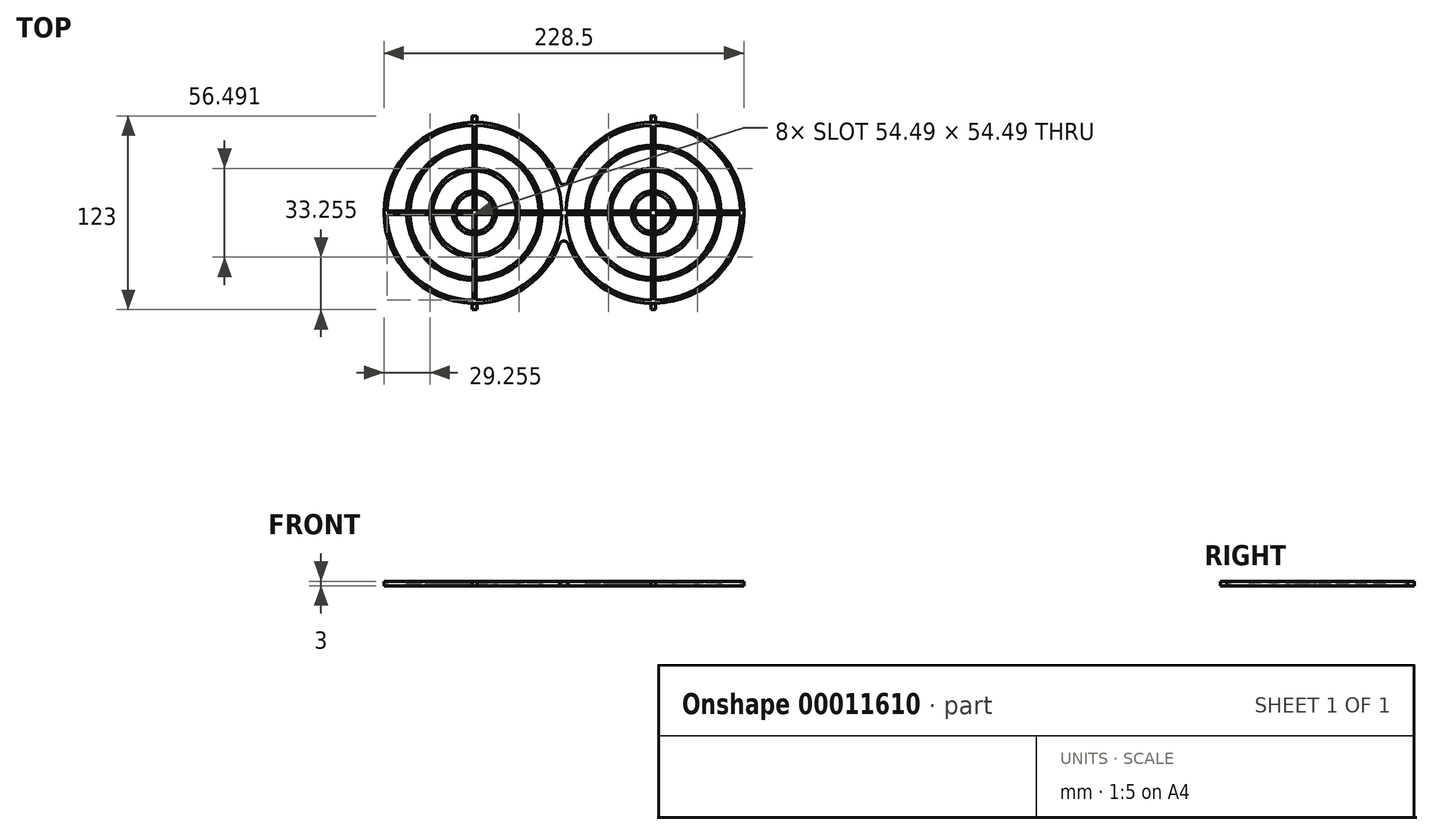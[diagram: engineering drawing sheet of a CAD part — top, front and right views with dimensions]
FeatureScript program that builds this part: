
annotation { "Feature Type Name" : "Feature", "Feature Type Description" : "" }
export const myFeature = defineFeature(function(context is Context, id is Id, definition is map)
    precondition{}
    {
        {
            var Q0;
            Q0=qCreatedBy(makeId("Top.planeOp"),FACE);
            var sketch = newSketch(context, id + "F0", { "sketchPlane" : qUnion([Q0])});
            skArc(sketch, "E0", {"start": v(-35.15, 19.67) * mm, "mid": v(-55.59, 46.67) * mm, "end": v(-87.68, 57.48) * mm});
            skArc(sketch, "E1", {"start": v(-29.71, -19.67) * mm, "mid": v(-9.27, -46.67) * mm, "end": v(22.82, -57.48) * mm});
            skArc(sketch, "E2", {"start": v(-35.15, 19.67) * mm, "mid": v(-32.43, 17.94) * mm, "end": v(-29.71, 19.67) * mm});
            skArc(sketch, "E3", {"start": v(-29.71, -19.67) * mm, "mid": v(-32.43, -17.94) * mm, "end": v(-35.15, -19.67) * mm});
            skArc(sketch, "E4", {"start": v(-31.17, -1) * mm, "mid": v(-14.92, -39.24) * mm, "end": v(23.32, -55.5) * mm});
            skArc(sketch, "E5", {"start": v(25.32, -42.99) * mm, "mid": v(54.73, -30.4) * mm, "end": v(67.3, -1) * mm});
            skArc(sketch, "E6", {"start": v(25.32, -40.99) * mm, "mid": v(53.31, -29) * mm, "end": v(65.3, -1) * mm});
            skArc(sketch, "E7", {"start": v(25.32, -28.48) * mm, "mid": v(44.47, -20.15) * mm, "end": v(52.8, -1) * mm});
            skArc(sketch, "E8", {"start": v(25.32, -26.48) * mm, "mid": v(43.06, -18.74) * mm, "end": v(50.8, -1) * mm});
            skArc(sketch, "E9", {"start": v(25.32, -13.96) * mm, "mid": v(34.22, -9.9) * mm, "end": v(38.28, -1) * mm});
            skArc(sketch, "E10", {"start": v(25.32, -11.96) * mm, "mid": v(32.8, -8.49) * mm, "end": v(36.28, -1) * mm});
            skArc(sketch, "E11", {"start": v(-90.18, 55.5) * mm, "mid": v(-128.42, 39.24) * mm, "end": v(-144.67, 1) * mm});
            skArc(sketch, "E12", {"start": v(-90.18, 42.99) * mm, "mid": v(-119.59, 30.4) * mm, "end": v(-132.17, 1) * mm});
            skArc(sketch, "E13", {"start": v(-90.18, 40.99) * mm, "mid": v(-118.17, 29) * mm, "end": v(-130.17, 1) * mm});
            skArc(sketch, "E14", {"start": v(-90.18, 28.48) * mm, "mid": v(-109.33, 20.15) * mm, "end": v(-117.66, 1) * mm});
            skArc(sketch, "E15", {"start": v(-90.18, 26.48) * mm, "mid": v(-107.92, 18.74) * mm, "end": v(-115.66, 1) * mm});
            skArc(sketch, "E16", {"start": v(-90.18, 13.96) * mm, "mid": v(-99.08, 9.9) * mm, "end": v(-103.14, 1) * mm});
            skArc(sketch, "E17", {"start": v(-90.18, 11.96) * mm, "mid": v(-97.67, 8.49) * mm, "end": v(-101.14, 1) * mm});
            skLineSegment(sketch, "E18.bottom", {"start": v(-88.18, 1) * mm, "end": v(-33.69, 1) * mm});
            skLineSegment(sketch, "E18.top", {"start": v(-88.18, -1) * mm, "end": v(-33.69, -1) * mm});
            skLineSegment(sketch, "E19.bottom", {"start": v(-90.18, 1) * mm, "end": v(-144.67, 1) * mm});
            skLineSegment(sketch, "E19.top", {"start": v(-90.18, -1) * mm, "end": v(-144.67, -1) * mm});
            skLineSegment(sketch, "E20.bottom", {"start": v(25.32, 1) * mm, "end": v(79.81, 1) * mm});
            skLineSegment(sketch, "E20.top", {"start": v(25.32, -1) * mm, "end": v(79.81, -1) * mm});
            skLineSegment(sketch, "E21.left", {"start": v(23.32, 1) * mm, "end": v(23.32, 55.5) * mm});
            skLineSegment(sketch, "E21.right", {"start": v(25.32, 1) * mm, "end": v(25.32, 55.5) * mm});
            skLineSegment(sketch, "E22.left", {"start": v(23.32, -1) * mm, "end": v(23.32, -55.5) * mm});
            skLineSegment(sketch, "E22.right", {"start": v(25.32, -1) * mm, "end": v(25.32, -55.5) * mm});
            skLineSegment(sketch, "E23.left", {"start": v(-88.18, 1) * mm, "end": v(-88.18, 55.5) * mm});
            skLineSegment(sketch, "E23.right", {"start": v(-90.18, 1) * mm, "end": v(-90.18, 55.5) * mm});
            skLineSegment(sketch, "E24.left", {"start": v(-90.18, -1) * mm, "end": v(-90.18, -55.5) * mm});
            skLineSegment(sketch, "E24.right", {"start": v(-88.18, -1) * mm, "end": v(-88.18, -55.5) * mm});
            skLineSegment(sketch, "E25.top", {"start": v(-87.68, 61.5) * mm, "end": v(-90.68, 61.5) * mm});
            skLineSegment(sketch, "E25.left", {"start": v(-87.68, 57.48) * mm, "end": v(-87.68, 61.5) * mm});
            skLineSegment(sketch, "E25.right", {"start": v(-90.68, 57.48) * mm, "end": v(-90.68, 61.5) * mm});
            skLineSegment(sketch, "E26.top", {"start": v(-87.68, -61.5) * mm, "end": v(-90.68, -61.5) * mm});
            skLineSegment(sketch, "E26.left", {"start": v(-87.68, -57.48) * mm, "end": v(-87.68, -61.5) * mm});
            skLineSegment(sketch, "E26.right", {"start": v(-90.68, -57.48) * mm, "end": v(-90.68, -61.5) * mm});
            skLineSegment(sketch, "E27.top", {"start": v(22.82, -61.5) * mm, "end": v(25.82, -61.5) * mm});
            skLineSegment(sketch, "E27.left", {"start": v(22.82, -57.48) * mm, "end": v(22.82, -61.5) * mm});
            skLineSegment(sketch, "E27.right", {"start": v(25.82, -57.48) * mm, "end": v(25.82, -61.5) * mm});
            skLineSegment(sketch, "E28.top", {"start": v(22.82, 61.5) * mm, "end": v(25.82, 61.5) * mm});
            skLineSegment(sketch, "E28.left", {"start": v(22.82, 57.48) * mm, "end": v(22.82, 61.5) * mm});
            skLineSegment(sketch, "E28.right", {"start": v(25.82, 57.48) * mm, "end": v(25.82, 61.5) * mm});
            skPoint(sketch, "E29.trimOffspring.end.orphan", {"position": v(-89.18, 61.5) * mm});
            skArc(sketch, "E30.trimOffspring", {"start": v(-90.68, 57.48) * mm, "mid": v(-146.68, 0) * mm, "end": v(-90.68, -57.48) * mm});
            skArc(sketch, "E31.trimOffspring", {"start": v(-101.14, -1) * mm, "mid": v(-97.67, -8.49) * mm, "end": v(-90.18, -11.96) * mm});
            skArc(sketch, "E32.trimOffspring", {"start": v(-103.14, -1) * mm, "mid": v(-99.08, -9.9) * mm, "end": v(-90.18, -13.96) * mm});
            skArc(sketch, "E33.trimOffspring", {"start": v(-115.66, -1) * mm, "mid": v(-107.92, -18.74) * mm, "end": v(-90.18, -26.48) * mm});
            skArc(sketch, "E34.trimOffspring", {"start": v(-117.66, -1) * mm, "mid": v(-109.33, -20.15) * mm, "end": v(-90.18, -28.48) * mm});
            skArc(sketch, "E35.trimOffspring", {"start": v(-144.67, -1) * mm, "mid": v(-128.42, -39.24) * mm, "end": v(-90.18, -55.5) * mm});
            skArc(sketch, "E36.trimOffspring", {"start": v(-132.17, -1) * mm, "mid": v(-119.59, -30.4) * mm, "end": v(-90.18, -42.99) * mm});
            skArc(sketch, "E37.trimOffspring", {"start": v(-130.17, -1) * mm, "mid": v(-118.17, -29) * mm, "end": v(-90.18, -40.99) * mm});
            skPoint(sketch, "E38.orphan", {"position": v(-89.18, -56) * mm});
            skPoint(sketch, "E39.orphan", {"position": v(-90.18, -56) * mm});
            skArc(sketch, "E40.trimOffspring", {"start": v(-88.18, -55.5) * mm, "mid": v(-49.94, -39.24) * mm, "end": v(-33.69, -1) * mm});
            skArc(sketch, "E41.trimOffspring", {"start": v(-87.68, -57.48) * mm, "mid": v(-55.59, -46.67) * mm, "end": v(-35.15, -19.67) * mm});
            skPoint(sketch, "E42.trimOffspring.end.orphan", {"position": v(-89.18, -61.5) * mm});
            skPoint(sketch, "E26.bottom.end.orphan", {"position": v(-88.18, -56) * mm});
            skArc(sketch, "E43.trimOffspring", {"start": v(-88.18, -11.96) * mm, "mid": v(-80.7, -8.49) * mm, "end": v(-77.22, -1) * mm});
            skArc(sketch, "E44.trimOffspring", {"start": v(-88.18, -13.96) * mm, "mid": v(-79.28, -9.9) * mm, "end": v(-75.22, -1) * mm});
            skArc(sketch, "E45.trimOffspring", {"start": v(-88.18, -26.48) * mm, "mid": v(-70.44, -18.74) * mm, "end": v(-62.7, -1) * mm});
            skArc(sketch, "E46.trimOffspring", {"start": v(-88.18, -28.48) * mm, "mid": v(-69.03, -20.15) * mm, "end": v(-60.7, -1) * mm});
            skArc(sketch, "E47.trimOffspring", {"start": v(-88.18, -42.99) * mm, "mid": v(-58.77, -30.4) * mm, "end": v(-46.2, -1) * mm});
            skArc(sketch, "E48.trimOffspring", {"start": v(-88.18, -40.99) * mm, "mid": v(-60.19, -29) * mm, "end": v(-48.2, -1) * mm});
            skArc(sketch, "E49.trimOffspring", {"start": v(-48.2, 1) * mm, "mid": v(-60.19, 29) * mm, "end": v(-88.18, 40.99) * mm});
            skArc(sketch, "E50.trimOffspring", {"start": v(-60.7, 1) * mm, "mid": v(-69.03, 20.15) * mm, "end": v(-88.18, 28.48) * mm});
            skArc(sketch, "E51.trimOffspring", {"start": v(-62.7, 1) * mm, "mid": v(-70.44, 18.74) * mm, "end": v(-88.18, 26.48) * mm});
            skArc(sketch, "E52.trimOffspring", {"start": v(-75.22, 1) * mm, "mid": v(-79.28, 9.9) * mm, "end": v(-88.18, 13.96) * mm});
            skArc(sketch, "E53.trimOffspring", {"start": v(-77.22, 1) * mm, "mid": v(-80.7, 8.49) * mm, "end": v(-88.18, 11.96) * mm});
            skArc(sketch, "E54.trimOffspring", {"start": v(-46.2, 1) * mm, "mid": v(-58.77, 30.4) * mm, "end": v(-88.18, 42.99) * mm});
            skArc(sketch, "E55.trimOffspring", {"start": v(-33.69, 1) * mm, "mid": v(-49.94, 39.24) * mm, "end": v(-88.18, 55.5) * mm});
            skLineSegment(sketch, "E56.trimOffspring", {"start": v(-31.17, 1) * mm, "end": v(23.32, 1) * mm});
            skLineSegment(sketch, "E57.trimOffspring", {"start": v(-31.17, -1) * mm, "end": v(23.32, -1) * mm});
            skArc(sketch, "E58.trimOffspring", {"start": v(25.32, -55.5) * mm, "mid": v(63.56, -39.24) * mm, "end": v(79.81, -1) * mm});
            skPoint(sketch, "E59.orphan", {"position": v(25.32, -56) * mm});
            skPoint(sketch, "E60.orphan", {"position": v(24.32, -56) * mm});
            skPoint(sketch, "E61.end.orphan", {"position": v(24.32, -61.5) * mm});
            skArc(sketch, "E62.trimOffspring", {"start": v(25.82, -57.48) * mm, "mid": v(81.82, 0) * mm, "end": v(25.82, 57.48) * mm});
            skPoint(sketch, "E63.start.orphan", {"position": v(23.32, -56) * mm});
            skArc(sketch, "E64.trimOffspring", {"start": v(23.32, 13.96) * mm, "mid": v(14.42, 9.9) * mm, "end": v(10.36, 1) * mm});
            skArc(sketch, "E65.trimOffspring", {"start": v(23.32, 11.96) * mm, "mid": v(15.83, 8.49) * mm, "end": v(12.36, 1) * mm});
            skArc(sketch, "E66.trimOffspring", {"start": v(23.32, 28.48) * mm, "mid": v(4.17, 20.15) * mm, "end": v(-4.16, 1) * mm});
            skArc(sketch, "E67.trimOffspring", {"start": v(23.32, 26.48) * mm, "mid": v(5.58, 18.74) * mm, "end": v(-2.16, 1) * mm});
            skArc(sketch, "E68.trimOffspring", {"start": v(23.32, 42.99) * mm, "mid": v(-6.09, 30.4) * mm, "end": v(-18.67, 1) * mm});
            skArc(sketch, "E69.trimOffspring", {"start": v(23.32, 40.99) * mm, "mid": v(-4.67, 29) * mm, "end": v(-16.67, 1) * mm});
            skArc(sketch, "E70.trimOffspring", {"start": v(23.32, 55.5) * mm, "mid": v(-14.92, 39.24) * mm, "end": v(-31.17, 1) * mm});
            skPoint(sketch, "E71.trimOffspring.end.orphan", {"position": v(24.32, 61.5) * mm});
            skArc(sketch, "E72.trimOffspring", {"start": v(22.82, 57.48) * mm, "mid": v(-9.27, 46.67) * mm, "end": v(-29.71, 19.67) * mm});
            skArc(sketch, "E73.trimOffspring", {"start": v(65.3, 1) * mm, "mid": v(53.31, 29) * mm, "end": v(25.32, 40.99) * mm});
            skArc(sketch, "E74.trimOffspring", {"start": v(67.3, 1) * mm, "mid": v(54.73, 30.4) * mm, "end": v(25.32, 42.99) * mm});
            skArc(sketch, "E75.trimOffspring", {"start": v(79.81, 1) * mm, "mid": v(63.56, 39.24) * mm, "end": v(25.32, 55.5) * mm});
            skArc(sketch, "E76.trimOffspring", {"start": v(52.8, 1) * mm, "mid": v(44.47, 20.15) * mm, "end": v(25.32, 28.48) * mm});
            skArc(sketch, "E77.trimOffspring", {"start": v(50.8, 1) * mm, "mid": v(43.06, 18.74) * mm, "end": v(25.32, 26.48) * mm});
            skArc(sketch, "E78.trimOffspring", {"start": v(38.28, 1) * mm, "mid": v(34.22, 9.9) * mm, "end": v(25.32, 13.96) * mm});
            skArc(sketch, "E79.trimOffspring", {"start": v(36.28, 1) * mm, "mid": v(32.8, 8.49) * mm, "end": v(25.32, 11.96) * mm});
            skArc(sketch, "E80.trimOffspring", {"start": v(12.36, -1) * mm, "mid": v(15.83, -8.49) * mm, "end": v(23.32, -11.96) * mm});
            skArc(sketch, "E81.trimOffspring", {"start": v(10.36, -1) * mm, "mid": v(14.42, -9.9) * mm, "end": v(23.32, -13.96) * mm});
            skArc(sketch, "E82.trimOffspring", {"start": v(-2.16, -1) * mm, "mid": v(5.58, -18.74) * mm, "end": v(23.32, -26.48) * mm});
            skArc(sketch, "E83.trimOffspring", {"start": v(-4.16, -1) * mm, "mid": v(4.17, -20.15) * mm, "end": v(23.32, -28.48) * mm});
            skArc(sketch, "E84.trimOffspring", {"start": v(-16.67, -1) * mm, "mid": v(-4.67, -29) * mm, "end": v(23.32, -40.99) * mm});
            skArc(sketch, "E85.trimOffspring", {"start": v(-18.67, -1) * mm, "mid": v(-6.09, -30.4) * mm, "end": v(23.32, -42.99) * mm});
            skSolve(sketch);
        }
        {
            var Q0;
            Q0=makeQuery(id+"F0.imprint","IMPRINT",FACE,{"disambiguationData":[TD([[makeQuery(id+"F0.imprint","IMPRINT",EDGE,{"derivedFrom":sQuery(id+"F0.wireOp",EDGE,"E0")}),1.0]])]});
            extrude(context, id + "F1", {"entities" : qUnion([Q0]), "depth" : 3 * mm});
        }
        {
            var Q0;
            {var subQ2=sQuery(id+"F0.wireOp",EDGE,"E12");Q0=makeQuery(id+"F0.imprint","IMPRINT",FACE,{"disambiguationData":[TD([[makeQuery(id+"F0.imprint","IMPRINT",EDGE,{"derivedFrom":subQ2}),1.0]])]});}
            var Q1;
            {var subQ2=sQuery(id+"F0.wireOp",EDGE,"E14");Q1=makeQuery(id+"F0.imprint","IMPRINT",FACE,{"disambiguationData":[TD([[makeQuery(id+"F0.imprint","IMPRINT",EDGE,{"derivedFrom":subQ2}),1.0]])]});}
            var Q2;
            {var subQ2=sQuery(id+"F0.wireOp",EDGE,"E16");Q2=makeQuery(id+"F0.imprint","IMPRINT",FACE,{"disambiguationData":[TD([[makeQuery(id+"F0.imprint","IMPRINT",EDGE,{"derivedFrom":subQ2}),1.0]])]});}
            var Q3;
            {var subQ1=sQuery(id+"F0.wireOp",EDGE,"E52.trimOffspring");Q3=makeQuery(id+"F0.imprint","IMPRINT",FACE,{"disambiguationData":[TD([[makeQuery(id+"F0.imprint","IMPRINT",EDGE,{"derivedFrom":subQ1}),1.0]])]});}
            var Q4;
            {var subQ1=sQuery(id+"F0.wireOp",EDGE,"E50.trimOffspring");Q4=makeQuery(id+"F0.imprint","IMPRINT",FACE,{"disambiguationData":[TD([[makeQuery(id+"F0.imprint","IMPRINT",EDGE,{"derivedFrom":subQ1}),1.0]])]});}
            var Q5;
            {var subQ1=sQuery(id+"F0.wireOp",EDGE,"E49.trimOffspring");Q5=makeQuery(id+"F0.imprint","IMPRINT",FACE,{"disambiguationData":[TD([[makeQuery(id+"F0.imprint","IMPRINT",EDGE,{"derivedFrom":subQ1}),-1.0]])]});}
            var Q6;
            {var subQ1=sQuery(id+"F0.wireOp",EDGE,"E43.trimOffspring");Q6=makeQuery(id+"F0.imprint","IMPRINT",FACE,{"disambiguationData":[TD([[makeQuery(id+"F0.imprint","IMPRINT",EDGE,{"derivedFrom":subQ1}),-1.0]])]});}
            var Q7;
            {var subQ1=sQuery(id+"F0.wireOp",EDGE,"E45.trimOffspring");Q7=makeQuery(id+"F0.imprint","IMPRINT",FACE,{"disambiguationData":[TD([[makeQuery(id+"F0.imprint","IMPRINT",EDGE,{"derivedFrom":subQ1}),-1.0]])]});}
            var Q8;
            {var subQ0=sQuery(id+"F0.wireOp",EDGE,"E47.trimOffspring");Q8=makeQuery(id+"F0.imprint","IMPRINT",FACE,{"disambiguationData":[TD([[makeQuery(id+"F0.imprint","IMPRINT",EDGE,{"derivedFrom":subQ0}),1.0]])]});}
            var Q9;
            {var subQ1=sQuery(id+"F0.wireOp",EDGE,"E31.trimOffspring");Q9=makeQuery(id+"F0.imprint","IMPRINT",FACE,{"disambiguationData":[TD([[makeQuery(id+"F0.imprint","IMPRINT",EDGE,{"derivedFrom":subQ1}),-1.0]])]});}
            var Q10;
            {var subQ1=sQuery(id+"F0.wireOp",EDGE,"E33.trimOffspring");Q10=makeQuery(id+"F0.imprint","IMPRINT",FACE,{"disambiguationData":[TD([[makeQuery(id+"F0.imprint","IMPRINT",EDGE,{"derivedFrom":subQ1}),-1.0]])]});}
            var Q11;
            {var subQ1=sQuery(id+"F0.wireOp",EDGE,"E36.trimOffspring");Q11=makeQuery(id+"F0.imprint","IMPRINT",FACE,{"disambiguationData":[TD([[makeQuery(id+"F0.imprint","IMPRINT",EDGE,{"derivedFrom":subQ1}),1.0]])]});}
            var Q12;
            {var subQ2=sQuery(id+"F0.wireOp",EDGE,"E68.trimOffspring");Q12=makeQuery(id+"F0.imprint","IMPRINT",FACE,{"disambiguationData":[TD([[makeQuery(id+"F0.imprint","IMPRINT",EDGE,{"derivedFrom":subQ2}),1.0]])]});}
            var Q13;
            {var subQ0=sQuery(id+"F0.wireOp",EDGE,"E66.trimOffspring");Q13=makeQuery(id+"F0.imprint","IMPRINT",FACE,{"disambiguationData":[TD([[makeQuery(id+"F0.imprint","IMPRINT",EDGE,{"derivedFrom":subQ0}),1.0]])]});}
            var Q14;
            {var subQ1=sQuery(id+"F0.wireOp",EDGE,"E73.trimOffspring");Q14=makeQuery(id+"F0.imprint","IMPRINT",FACE,{"disambiguationData":[TD([[makeQuery(id+"F0.imprint","IMPRINT",EDGE,{"derivedFrom":subQ1}),-1.0]])]});}
            var Q15;
            {var subQ1=sQuery(id+"F0.wireOp",EDGE,"E76.trimOffspring");Q15=makeQuery(id+"F0.imprint","IMPRINT",FACE,{"disambiguationData":[TD([[makeQuery(id+"F0.imprint","IMPRINT",EDGE,{"derivedFrom":subQ1}),1.0]])]});}
            var Q16;
            {var subQ1=sQuery(id+"F0.wireOp",EDGE,"E78.trimOffspring");Q16=makeQuery(id+"F0.imprint","IMPRINT",FACE,{"disambiguationData":[TD([[makeQuery(id+"F0.imprint","IMPRINT",EDGE,{"derivedFrom":subQ1}),1.0]])]});}
            var Q17;
            {var subQ1=sQuery(id+"F0.wireOp",EDGE,"E64.trimOffspring");Q17=makeQuery(id+"F0.imprint","IMPRINT",FACE,{"disambiguationData":[TD([[makeQuery(id+"F0.imprint","IMPRINT",EDGE,{"derivedFrom":subQ1}),1.0]])]});}
            var Q18;
            {var subQ1=sQuery(id+"F0.wireOp",EDGE,"E80.trimOffspring");Q18=makeQuery(id+"F0.imprint","IMPRINT",FACE,{"disambiguationData":[TD([[makeQuery(id+"F0.imprint","IMPRINT",EDGE,{"derivedFrom":subQ1}),-1.0]])]});}
            var Q19;
            {var subQ1=sQuery(id+"F0.wireOp",EDGE,"E82.trimOffspring");Q19=makeQuery(id+"F0.imprint","IMPRINT",FACE,{"disambiguationData":[TD([[makeQuery(id+"F0.imprint","IMPRINT",EDGE,{"derivedFrom":subQ1}),-1.0]])]});}
            var Q20;
            {var subQ1=sQuery(id+"F0.wireOp",EDGE,"E84.trimOffspring");Q20=makeQuery(id+"F0.imprint","IMPRINT",FACE,{"disambiguationData":[TD([[makeQuery(id+"F0.imprint","IMPRINT",EDGE,{"derivedFrom":subQ1}),-1.0]])]});}
            var Q21;
            {var subQ2=sQuery(id+"F0.wireOp",EDGE,"E9");Q21=makeQuery(id+"F0.imprint","IMPRINT",FACE,{"disambiguationData":[TD([[makeQuery(id+"F0.imprint","IMPRINT",EDGE,{"derivedFrom":subQ2}),1.0]])]});}
            var Q22;
            {var subQ2=sQuery(id+"F0.wireOp",EDGE,"E7");Q22=makeQuery(id+"F0.imprint","IMPRINT",FACE,{"disambiguationData":[TD([[makeQuery(id+"F0.imprint","IMPRINT",EDGE,{"derivedFrom":subQ2}),1.0]])]});}
            var Q23;
            {var subQ2=sQuery(id+"F0.wireOp",EDGE,"E5");Q23=makeQuery(id+"F0.imprint","IMPRINT",FACE,{"disambiguationData":[TD([[makeQuery(id+"F0.imprint","IMPRINT",EDGE,{"derivedFrom":subQ2}),1.0]])]});}
            extrude(context, id + "F2", {"entities" : qUnion([Q0, Q1, Q2, Q3, Q4, Q5, Q6, Q7, Q8, Q9, Q10, Q11, Q12, Q13, Q14, Q15, Q16, Q17, Q18, Q19, Q20, Q21, Q22, Q23]), "operationType" : NewBodyOperationType.ADD, "depth" : 2 * mm});
        }
        {
            var Q0;
            Q0=makeQuery(id+"F1.opExtrude","SWEPT_FACE",FACE,{"disambiguationData":[OSD([sQuery(id+"F0.wireOp",EDGE,"E26.top")])]});
            var sketch = newSketch(context, id + "F3", { "sketchPlane" : qUnion([Q0])});
            skCircle(sketch, "E86", {"center": v(-89.18, 1.5) * mm, "radius": 1.5 * mm});
            skCircle(sketch, "E87", {"center": v(24.32, 1.5) * mm, "radius": 1.5 * mm});
            skLineSegment(sketch, "E88.bottom", {"start": v(22.82, 3) * mm, "end": v(25.82, 3) * mm});
            skLineSegment(sketch, "E88.top", {"start": v(22.82, 0) * mm, "end": v(25.82, 0) * mm});
            skLineSegment(sketch, "E88.left", {"start": v(22.82, 3) * mm, "end": v(22.82, 0) * mm});
            skLineSegment(sketch, "E88.right", {"start": v(25.82, 3) * mm, "end": v(25.82, 0) * mm});
            skLineSegment(sketch, "E89.bottom", {"start": v(-90.68, 3) * mm, "end": v(-87.68, 3) * mm});
            skLineSegment(sketch, "E89.top", {"start": v(-90.68, 0) * mm, "end": v(-87.68, 0) * mm});
            skLineSegment(sketch, "E89.left", {"start": v(-90.68, 3) * mm, "end": v(-90.68, 0) * mm});
            skLineSegment(sketch, "E89.right", {"start": v(-87.68, 3) * mm, "end": v(-87.68, 0) * mm});
            skSolve(sketch);
        }
        {
            var Q0;
            {var subQ1=sQuery(id+"F3.wireOp",EDGE,"E86");var subQ3=sQuery(id+"F3.wireOp",EDGE,"E89.bottom");var subQ5=makeQuery(id+"F3.imprint","INTERSECT",VERTEX,{"derivedFrom":[subQ1,subQ3]});Q0=makeQuery(id+"F3.imprint","IMPRINT",FACE,{"disambiguationData":[TD([[makeQuery(id+"F3.imprint","IMPRINT",EDGE,{"disambiguationData":[TD([[subQ5,-1.0]])],"derivedFrom":subQ1}),-1.0]])]});}
            var Q1;
            {var subQ1=sQuery(id+"F3.wireOp",EDGE,"E86");var subQ3=sQuery(id+"F3.wireOp",EDGE,"E89.bottom");var subQ5=makeQuery(id+"F3.imprint","INTERSECT",VERTEX,{"derivedFrom":[subQ1,subQ3]});Q1=makeQuery(id+"F3.imprint","IMPRINT",FACE,{"disambiguationData":[TD([[makeQuery(id+"F3.imprint","IMPRINT",EDGE,{"disambiguationData":[TD([[subQ5,1.0]])],"derivedFrom":subQ1}),-1.0]])]});}
            var Q2;
            {var subQ0=sQuery(id+"F3.wireOp",EDGE,"E89.right");var subQ1=sQuery(id+"F3.wireOp",EDGE,"E86");var subQ2=makeQuery(id+"F3.imprint","INTERSECT",VERTEX,{"derivedFrom":[subQ1,subQ0]});Q2=makeQuery(id+"F3.imprint","IMPRINT",FACE,{"disambiguationData":[TD([[makeQuery(id+"F3.imprint","IMPRINT",EDGE,{"disambiguationData":[TD([[subQ2,1.0]])],"derivedFrom":subQ1}),-1.0]])]});}
            var Q3;
            {var subQ0=sQuery(id+"F3.wireOp",EDGE,"E89.left");var subQ1=sQuery(id+"F3.wireOp",EDGE,"E86");var subQ2=makeQuery(id+"F3.imprint","INTERSECT",VERTEX,{"derivedFrom":[subQ1,subQ0]});Q3=makeQuery(id+"F3.imprint","IMPRINT",FACE,{"disambiguationData":[TD([[makeQuery(id+"F3.imprint","IMPRINT",EDGE,{"disambiguationData":[TD([[subQ2,-1.0]])],"derivedFrom":subQ1}),-1.0]])]});}
            var Q4;
            {var subQ1=sQuery(id+"F3.wireOp",EDGE,"E87");var subQ3=sQuery(id+"F3.wireOp",EDGE,"E88.bottom");var subQ5=makeQuery(id+"F3.imprint","INTERSECT",VERTEX,{"derivedFrom":[subQ1,subQ3]});Q4=makeQuery(id+"F3.imprint","IMPRINT",FACE,{"disambiguationData":[TD([[makeQuery(id+"F3.imprint","IMPRINT",EDGE,{"disambiguationData":[TD([[subQ5,-1.0]])],"derivedFrom":subQ1}),-1.0]])]});}
            var Q5;
            {var subQ1=sQuery(id+"F3.wireOp",EDGE,"E87");var subQ3=sQuery(id+"F3.wireOp",EDGE,"E88.bottom");var subQ5=makeQuery(id+"F3.imprint","INTERSECT",VERTEX,{"derivedFrom":[subQ1,subQ3]});Q5=makeQuery(id+"F3.imprint","IMPRINT",FACE,{"disambiguationData":[TD([[makeQuery(id+"F3.imprint","IMPRINT",EDGE,{"disambiguationData":[TD([[subQ5,1.0]])],"derivedFrom":subQ1}),-1.0]])]});}
            var Q6;
            {var subQ0=sQuery(id+"F3.wireOp",EDGE,"E88.right");var subQ1=sQuery(id+"F3.wireOp",EDGE,"E87");var subQ2=makeQuery(id+"F3.imprint","INTERSECT",VERTEX,{"derivedFrom":[subQ1,subQ0]});Q6=makeQuery(id+"F3.imprint","IMPRINT",FACE,{"disambiguationData":[TD([[makeQuery(id+"F3.imprint","IMPRINT",EDGE,{"disambiguationData":[TD([[subQ2,1.0]])],"derivedFrom":subQ1}),-1.0]])]});}
            var Q7;
            {var subQ0=sQuery(id+"F3.wireOp",EDGE,"E88.left");var subQ1=sQuery(id+"F3.wireOp",EDGE,"E87");var subQ2=makeQuery(id+"F3.imprint","INTERSECT",VERTEX,{"derivedFrom":[subQ1,subQ0]});Q7=makeQuery(id+"F3.imprint","IMPRINT",FACE,{"disambiguationData":[TD([[makeQuery(id+"F3.imprint","IMPRINT",EDGE,{"disambiguationData":[TD([[subQ2,-1.0]])],"derivedFrom":subQ1}),-1.0]])]});}
            extrude(context, id + "F4", {"entities" : qUnion([Q0, Q1, Q2, Q3, Q4, Q5, Q6, Q7]), "operationType" : NewBodyOperationType.REMOVE, "oppositeDirection" : true, "depth" : 4 * mm});
        }
        {
            var Q0;
            Q0=makeQuery(id+"F1.opExtrude","SWEPT_FACE",FACE,{"disambiguationData":[OSD([sQuery(id+"F0.wireOp",EDGE,"E28.top")])]});
            var sketch = newSketch(context, id + "F5", { "sketchPlane" : qUnion([Q0])});
            skCircle(sketch, "E90", {"center": v(-24.32, 1.5) * mm, "radius": 1.5 * mm});
            skCircle(sketch, "E91", {"center": v(89.18, 1.5) * mm, "radius": 1.5 * mm});
            skLineSegment(sketch, "E92.bottom", {"start": v(-25.82, 3) * mm, "end": v(-22.82, 3) * mm});
            skLineSegment(sketch, "E92.top", {"start": v(-25.82, 0) * mm, "end": v(-22.82, 0) * mm});
            skLineSegment(sketch, "E92.left", {"start": v(-25.82, 3) * mm, "end": v(-25.82, 0) * mm});
            skLineSegment(sketch, "E92.right", {"start": v(-22.82, 3) * mm, "end": v(-22.82, 0) * mm});
            skLineSegment(sketch, "E93.rect.bottom", {"start": v(87.68, 3) * mm, "end": v(90.68, 3) * mm});
            skLineSegment(sketch, "E93.rect.top", {"start": v(87.68, 0) * mm, "end": v(90.68, 0) * mm});
            skLineSegment(sketch, "E93.rect.left", {"start": v(87.68, 3) * mm, "end": v(87.68, 0) * mm});
            skLineSegment(sketch, "E93.rect.right", {"start": v(90.68, 3) * mm, "end": v(90.68, 0) * mm});
            skSolve(sketch);
        }
        {
            var Q0;
            {var subQ1=sQuery(id+"F5.wireOp",EDGE,"E90");var subQ3=sQuery(id+"F5.wireOp",EDGE,"E92.bottom");var subQ5=makeQuery(id+"F5.imprint","INTERSECT",VERTEX,{"derivedFrom":[subQ1,subQ3]});Q0=makeQuery(id+"F5.imprint","IMPRINT",FACE,{"disambiguationData":[TD([[makeQuery(id+"F5.imprint","IMPRINT",EDGE,{"disambiguationData":[TD([[subQ5,-1.0]])],"derivedFrom":subQ1}),-1.0]])]});}
            var Q1;
            {var subQ1=sQuery(id+"F5.wireOp",EDGE,"E90");var subQ3=sQuery(id+"F5.wireOp",EDGE,"E92.bottom");var subQ5=makeQuery(id+"F5.imprint","INTERSECT",VERTEX,{"derivedFrom":[subQ1,subQ3]});Q1=makeQuery(id+"F5.imprint","IMPRINT",FACE,{"disambiguationData":[TD([[makeQuery(id+"F5.imprint","IMPRINT",EDGE,{"disambiguationData":[TD([[subQ5,1.0]])],"derivedFrom":subQ1}),-1.0]])]});}
            var Q2;
            {var subQ0=sQuery(id+"F5.wireOp",EDGE,"E92.right");var subQ1=sQuery(id+"F5.wireOp",EDGE,"E90");var subQ2=makeQuery(id+"F5.imprint","INTERSECT",VERTEX,{"derivedFrom":[subQ1,subQ0]});Q2=makeQuery(id+"F5.imprint","IMPRINT",FACE,{"disambiguationData":[TD([[makeQuery(id+"F5.imprint","IMPRINT",EDGE,{"disambiguationData":[TD([[subQ2,1.0]])],"derivedFrom":subQ1}),-1.0]])]});}
            var Q3;
            {var subQ0=sQuery(id+"F5.wireOp",EDGE,"E92.left");var subQ1=sQuery(id+"F5.wireOp",EDGE,"E90");var subQ2=makeQuery(id+"F5.imprint","INTERSECT",VERTEX,{"derivedFrom":[subQ1,subQ0]});Q3=makeQuery(id+"F5.imprint","IMPRINT",FACE,{"disambiguationData":[TD([[makeQuery(id+"F5.imprint","IMPRINT",EDGE,{"disambiguationData":[TD([[subQ2,-1.0]])],"derivedFrom":subQ1}),-1.0]])]});}
            var Q4;
            {var subQ1=sQuery(id+"F5.wireOp",EDGE,"E91");var subQ3=sQuery(id+"F5.wireOp",EDGE,"E93.rect.bottom");var subQ5=makeQuery(id+"F5.imprint","INTERSECT",VERTEX,{"derivedFrom":[subQ1,subQ3]});Q4=makeQuery(id+"F5.imprint","IMPRINT",FACE,{"disambiguationData":[TD([[makeQuery(id+"F5.imprint","IMPRINT",EDGE,{"disambiguationData":[TD([[subQ5,-1.0]])],"derivedFrom":subQ1}),-1.0]])]});}
            var Q5;
            {var subQ1=sQuery(id+"F5.wireOp",EDGE,"E91");var subQ3=sQuery(id+"F5.wireOp",EDGE,"E93.rect.bottom");var subQ5=makeQuery(id+"F5.imprint","INTERSECT",VERTEX,{"derivedFrom":[subQ1,subQ3]});Q5=makeQuery(id+"F5.imprint","IMPRINT",FACE,{"disambiguationData":[TD([[makeQuery(id+"F5.imprint","IMPRINT",EDGE,{"disambiguationData":[TD([[subQ5,1.0]])],"derivedFrom":subQ1}),-1.0]])]});}
            var Q6;
            {var subQ0=sQuery(id+"F5.wireOp",EDGE,"E93.rect.right");var subQ1=sQuery(id+"F5.wireOp",EDGE,"E91");var subQ2=makeQuery(id+"F5.imprint","INTERSECT",VERTEX,{"derivedFrom":[subQ1,subQ0]});Q6=makeQuery(id+"F5.imprint","IMPRINT",FACE,{"disambiguationData":[TD([[makeQuery(id+"F5.imprint","IMPRINT",EDGE,{"disambiguationData":[TD([[subQ2,1.0]])],"derivedFrom":subQ1}),-1.0]])]});}
            var Q7;
            {var subQ0=sQuery(id+"F5.wireOp",EDGE,"E93.rect.left");var subQ1=sQuery(id+"F5.wireOp",EDGE,"E91");var subQ2=makeQuery(id+"F5.imprint","INTERSECT",VERTEX,{"derivedFrom":[subQ1,subQ0]});Q7=makeQuery(id+"F5.imprint","IMPRINT",FACE,{"disambiguationData":[TD([[makeQuery(id+"F5.imprint","IMPRINT",EDGE,{"disambiguationData":[TD([[subQ2,-1.0]])],"derivedFrom":subQ1}),-1.0]])]});}
            extrude(context, id + "F6", {"entities" : qUnion([Q0, Q1, Q2, Q3, Q4, Q5, Q6, Q7]), "operationType" : NewBodyOperationType.REMOVE, "oppositeDirection" : true, "depth" : 4 * mm});
        }
    });
